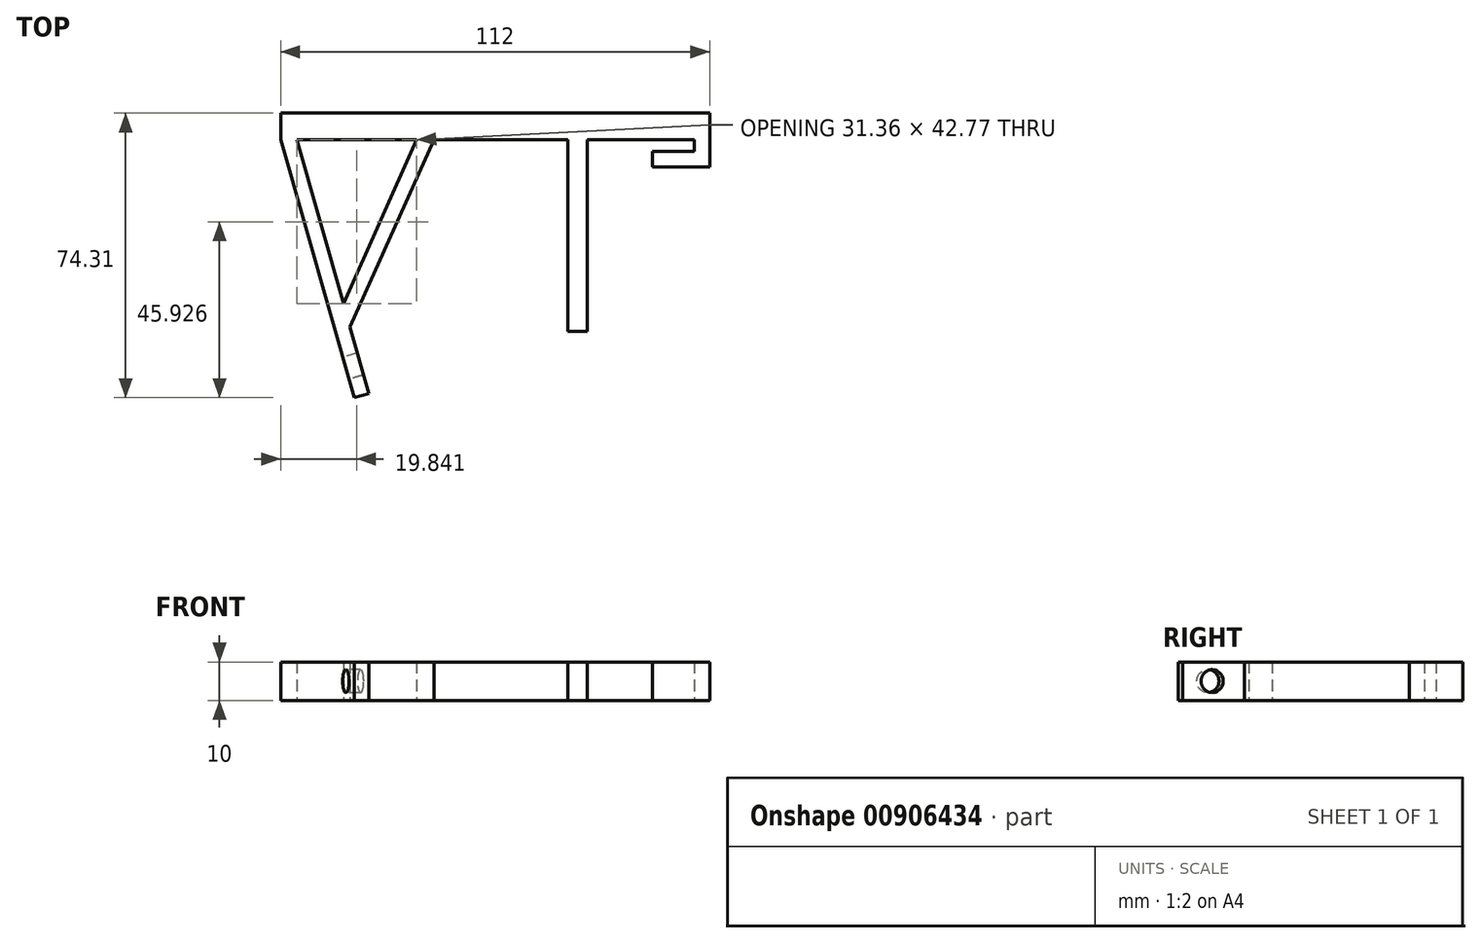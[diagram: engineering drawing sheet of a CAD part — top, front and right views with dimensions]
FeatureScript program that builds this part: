
annotation { "Feature Type Name" : "Feature", "Feature Type Description" : "" }
export const myFeature = defineFeature(function(context is Context, id is Id, definition is map)
    precondition{}
    {
        {
            var Q0;
            Q0=qCreatedBy(makeId("Top.planeOp"),FACE);
            var sketch = newSketch(context, id + "F0", { "sketchPlane" : qUnion([Q0])});
            skLineSegment(sketch, "E0.bottom", {"start": v(0, 0) * mm, "end": v(-80, 0) * mm});
            skLineSegment(sketch, "E0.top", {"start": v(0, 7) * mm, "end": v(-80, 7) * mm});
            skLineSegment(sketch, "E0.left", {"start": v(0, 0) * mm, "end": v(0, 7) * mm});
            skLineSegment(sketch, "E0.right", {"start": v(-80, 0) * mm, "end": v(-80, 7) * mm});
            skLineSegment(sketch, "E1.bottom", {"start": v(0, 0) * mm, "end": v(-5, 0) * mm});
            skLineSegment(sketch, "E1.top", {"start": v(0, -50) * mm, "end": v(-5, -50) * mm});
            skLineSegment(sketch, "E1.left", {"start": v(0, 0) * mm, "end": v(0, -50) * mm});
            skLineSegment(sketch, "E1.right", {"start": v(-5, 0) * mm, "end": v(-5, -50) * mm});
            skLineSegment(sketch, "E2", {"start": v(-80, 0) * mm, "end": v(-60.77, -67.3) * mm});
            skLineSegment(sketch, "E3", {"start": v(-60.77, -67.3) * mm, "end": v(-56.92, -66.2) * mm});
            skLineSegment(sketch, "E4", {"start": v(-56.92, -66.2) * mm, "end": v(-75.84, 0) * mm});
            skLineSegment(sketch, "E5.bottom", {"start": v(0, 0) * mm, "end": v(0, 0) * mm});
            skLineSegment(sketch, "E5.top", {"start": v(0, 7) * mm, "end": v(0, 7) * mm});
            skLineSegment(sketch, "E6.bottom", {"start": v(0, 7) * mm, "end": v(32, 7) * mm});
            skLineSegment(sketch, "E6.top", {"start": v(0, 0) * mm, "end": v(32, 0) * mm});
            skLineSegment(sketch, "E6.left", {"start": v(0, 7) * mm, "end": v(0, 0) * mm});
            skLineSegment(sketch, "E6.right", {"start": v(32, 7) * mm, "end": v(32, 0) * mm});
            skLineSegment(sketch, "E7.bottom", {"start": v(32, 0) * mm, "end": v(28, 0) * mm});
            skLineSegment(sketch, "E7.top", {"start": v(32, -3) * mm, "end": v(28, -3) * mm});
            skLineSegment(sketch, "E7.left", {"start": v(32, 0) * mm, "end": v(32, -3) * mm});
            skLineSegment(sketch, "E7.right", {"start": v(28, 0) * mm, "end": v(28, -3) * mm});
            skLineSegment(sketch, "E8.bottom", {"start": v(32, -3) * mm, "end": v(17, -3) * mm});
            skLineSegment(sketch, "E8.top", {"start": v(32, -7) * mm, "end": v(17, -7) * mm});
            skLineSegment(sketch, "E8.left", {"start": v(32, -3) * mm, "end": v(32, -7) * mm});
            skLineSegment(sketch, "E8.right", {"start": v(17, -3) * mm, "end": v(17, -7) * mm});
            skLineSegment(sketch, "E9", {"start": v(-44.48, 0) * mm, "end": v(-63.62, -42.77) * mm});
            skLineSegment(sketch, "E10", {"start": v(-63.62, -42.77) * mm, "end": v(-61.87, -48.87) * mm});
            skLineSegment(sketch, "E11", {"start": v(-61.87, -48.87) * mm, "end": v(-40, 0) * mm});
            skLineSegment(sketch, "E12", {"start": v(-40, 0) * mm, "end": v(-44.48, 0) * mm});
            skSolve(sketch);
        }
        {
            var Q0;
            Q0 = qSketchRegion(id + "F0", true);
            extrude(context, id + "F1", {"entities" : qUnion([Q0]), "depth" : 10 * mm, "offsetDistance" : 25 * mm});
        }
        {
            var Q0;
            Q0=makeQuery(id+"F1.opExtrude","SWEPT_FACE",FACE,{"disambiguationData":[OSD([sQuery(id+"F0.wireOp",EDGE,"E2")])]});
            var sketch = newSketch(context, id + "F2", { "sketchPlane" : qUnion([Q0])});
            skLineSegment(sketch, "E13", {"start": v(48.02, 0) * mm, "end": v(38.02, 0) * mm});
            skLineSegment(sketch, "E14", {"start": v(38.02, 0) * mm, "end": v(38.02, 5) * mm});
            skSolve(sketch);
        }
        {
            var Q0;
            {var subQ3=sQuery(id+"F2.wireOp",EDGE,"E13");Q0=makeQuery(id+"F2.imprint","IMPRINT",FACE,{"disambiguationData":[TD([[makeQuery(id+"F2.imprint","IMPRINT",EDGE,{"derivedFrom":subQ3}),1.0]])]});}
            var sketch = newSketch(context, id + "F3", { "sketchPlane" : qUnion([Q0])});
            skCircle(sketch, "E15", {"center": v(39.96, 5.03) * mm, "radius": 3 * mm});
            skSolve(sketch);
        }
        {
            var Q0;
            Q0 = qSketchRegion(id + "F3", true);
            extrude(context, id + "F4", {"entities" : qUnion([Q0]), "operationType" : NewBodyOperationType.REMOVE, "oppositeDirection" : true, "depth" : 10 * mm, "offsetDistance" : 25 * mm});
        }
    });
